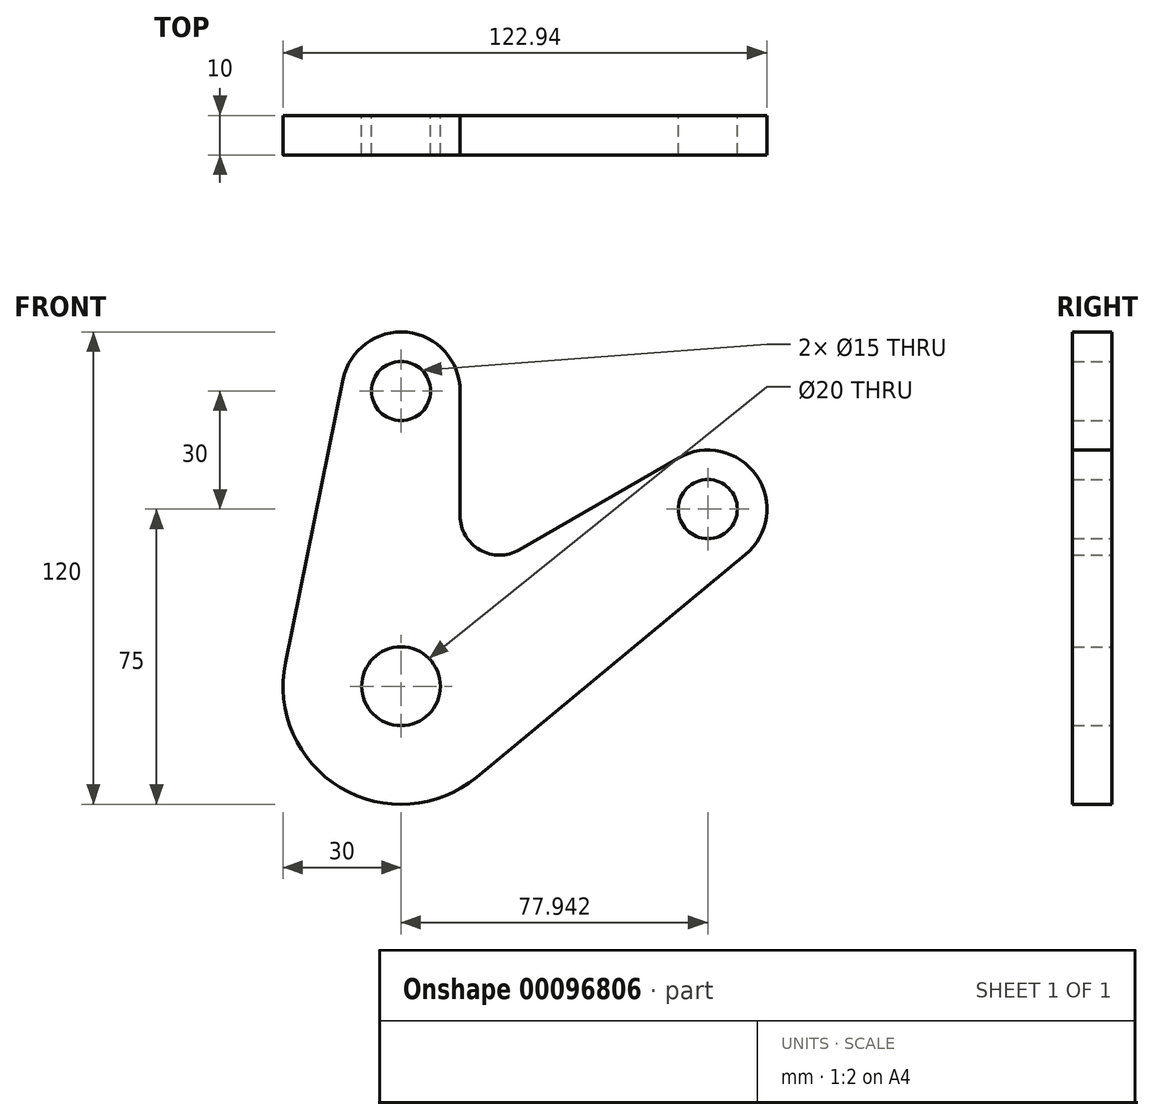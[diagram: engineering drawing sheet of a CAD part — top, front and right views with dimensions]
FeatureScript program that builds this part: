
annotation { "Feature Type Name" : "Feature", "Feature Type Description" : "" }
export const myFeature = defineFeature(function(context is Context, id is Id, definition is map)
    precondition{}
    {
        {
            var Q0;
            Q0=qCreatedBy(makeId("Front.planeOp"),FACE);
            var sketch = newSketch(context, id + "F0", { "sketchPlane" : qUnion([Q0])});
            skCircle(sketch, "E0", {"center": v(0, 0) * mm, "radius": 10 * mm});
            skCircle(sketch, "E1", {"center": v(0, 75) * mm, "radius": 7.5 * mm});
            skCircle(sketch, "E2", {"center": v(77.94, 45) * mm, "radius": 7.5 * mm});
            skLineSegment(sketch, "E3", {"start": v(-29.4, 6) * mm, "end": v(-14.7, 78) * mm});
            skArc(sketch, "E4", {"start": v(87.5, 33.44) * mm, "mid": v(90.26, 53.56) * mm, "end": v(70.44, 58) * mm});
            skLineSegment(sketch, "E5", {"start": v(16.23, -25.5) * mm, "end": v(87.5, 33.44) * mm});
            skLineSegment(sketch, "E6", {"start": v(0, 75) * mm, "end": v(0, 0) * mm, "construction": true});
            skLineSegment(sketch, "E7", {"start": v(0, 0) * mm, "end": v(77.94, 45) * mm, "construction": true});
            skArc(sketch, "E8", {"start": v(15, 75) * mm, "mid": v(1.5, 89.92) * mm, "end": v(-14.7, 78) * mm});
            skArc(sketch, "E9", {"start": v(-29.4, 6) * mm, "mid": v(-15.44, -25.72) * mm, "end": v(19.12, -23.12) * mm});
            skLineSegment(sketch, "E10", {"start": v(15, 75) * mm, "end": v(15, 43.3) * mm});
            skLineSegment(sketch, "E11", {"start": v(30, 34.64) * mm, "end": v(70.44, 58) * mm});
            skArc(sketch, "E12", {"start": v(15, 43.3) * mm, "mid": v(20, 34.64) * mm, "end": v(30, 34.64) * mm});
            skSolve(sketch);
        }
        {
            var Q0;
            Q0 = qSketchRegion(id + "F0", true);
            extrude(context, id + "F1", {"entities" : qUnion([Q0]), "depth" : 10 * mm});
        }
    });
